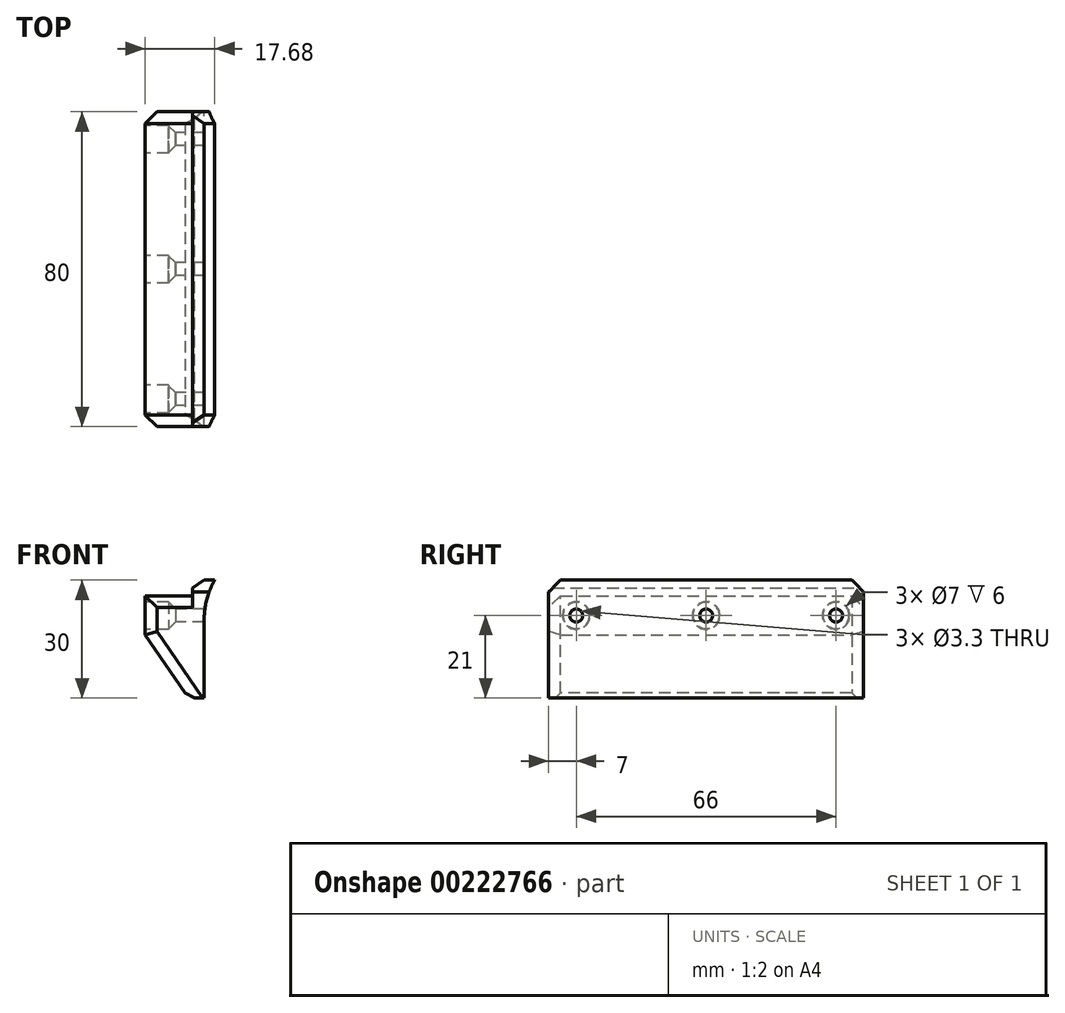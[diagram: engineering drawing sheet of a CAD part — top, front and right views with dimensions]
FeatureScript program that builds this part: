
annotation { "Feature Type Name" : "Feature", "Feature Type Description" : "" }
export const myFeature = defineFeature(function(context is Context, id is Id, definition is map)
    precondition{}
    {
        {
            var Q0;
            Q0=qCreatedBy(makeId("Front.planeOp"),FACE);
            var sketch = newSketch(context, id + "F0", { "sketchPlane" : qUnion([Q0])});
            skLineSegment(sketch, "E0", {"start": v(0, 0) * mm, "end": v(-15, 0) * mm});
            skLineSegment(sketch, "E1", {"start": v(-15, 0) * mm, "end": v(-15, -10) * mm});
            skLineSegment(sketch, "E2", {"start": v(-15, -10) * mm, "end": v(-4, -26) * mm});
            skLineSegment(sketch, "E3", {"start": v(-4, -26) * mm, "end": v(0, -26) * mm});
            skLineSegment(sketch, "E4", {"start": v(0, -26) * mm, "end": v(0, 0) * mm});
            skSolve(sketch);
        }
        {
            var Q0;
            Q0=makeQuery(id+"F0.imprint","IMPRINT",FACE,{"disambiguationData":[TD([[makeQuery(id+"F0.imprint","IMPRINT",EDGE,{"derivedFrom":sQuery(id+"F0.wireOp",EDGE,"E0")}),1.0]])]});
            extrude(context, id + "F1", {"entities" : qUnion([Q0]), "endBound" : BoundingType.SYMMETRIC, "depth" : 80 * mm});
        }
        {
            var Q0;
            Q0=makeQuery(id+"F1.opExtrude","SWEPT_FACE",FACE,{"disambiguationData":[OSD([sQuery(id+"F0.wireOp",EDGE,"E1")])]});
            var sketch = newSketch(context, id + "F2", { "sketchPlane" : qUnion([Q0])});
            skLineSegment(sketch, "E5.0", {"start": v(40, 0) * mm, "end": v(-40, 0) * mm, "construction": true});
            skCircle(sketch, "E6", {"center": v(-33, -5) * mm, "radius": 3.5 * mm});
            skCircle(sketch, "E7", {"center": v(33, -5) * mm, "radius": 3.5 * mm});
            skCircle(sketch, "E8", {"center": v(0, -5) * mm, "radius": 3.5 * mm});
            skSolve(sketch);
        }
        {
            var Q0;
            Q0=qCreatedBy(makeId("Front.planeOp"),FACE);
            var sketch = newSketch(context, id + "F3", { "sketchPlane" : qUnion([Q0])});
            skArc(sketch, "E9", {"start": v(2.68, 4) * mm, "mid": v(0.68, -0.82) * mm, "end": v(0, -6) * mm});
            skLineSegment(sketch, "E10", {"start": v(2.68, 4) * mm, "end": v(0, 4) * mm});
            skLineSegment(sketch, "E11", {"start": v(0, 4) * mm, "end": v(-3, 2) * mm});
            skLineSegment(sketch, "E12", {"start": v(0, 0) * mm, "end": v(0, -6) * mm});
            skLineSegment(sketch, "E13", {"start": v(-3, 2) * mm, "end": v(-3, 0) * mm});
            skLineSegment(sketch, "E14", {"start": v(-3, 0) * mm, "end": v(0, 0) * mm});
            skSolve(sketch);
        }
        {
            var Q0;
            Q0=qSketchRegion(id+"F2",true);
            extrude(context, id + "F4", {"entities" : qUnion([Q0]), "operationType" : NewBodyOperationType.REMOVE, "oppositeDirection" : true, "depth" : 6 * mm});
        }
        {
            var Q0;
            Q0 = qSketchRegion(id + "F3", true);
            var Q1;
            Q1=makeQuery(id+"F1.opExtrude","CAP_FACE",FACE,{"disambiguationData":[OSD([sQuery(id+"F0.wireOp",EDGE,"E0"),sQuery(id+"F0.wireOp",EDGE,"E1"),sQuery(id+"F0.wireOp",EDGE,"E2"),sQuery(id+"F0.wireOp",EDGE,"E3"),sQuery(id+"F0.wireOp",EDGE,"E4")])],"isStart":true});
            var Q2;
            Q2=makeQuery(id+"F1.opExtrude","CAP_FACE",FACE,{"disambiguationData":[OSD([sQuery(id+"F0.wireOp",EDGE,"E0"),sQuery(id+"F0.wireOp",EDGE,"E1"),sQuery(id+"F0.wireOp",EDGE,"E2"),sQuery(id+"F0.wireOp",EDGE,"E3"),sQuery(id+"F0.wireOp",EDGE,"E4")])],"isStart":false});
            extrude(context, id + "F5", {"entities" : qUnion([Q0]), "operationType" : NewBodyOperationType.ADD, "endBound" : BoundingType.SYMMETRIC, "endBoundEntityFace" : qUnion([Q1]), "depth" : 80 * mm, "hasSecondDirection" : true, "secondDirectionBound" : SecondDirectionBoundingType.UP_TO_SURFACE, "secondDirectionOppositeDirection" : true, "secondDirectionBoundEntityFace" : qUnion([Q2]), "secondDirectionDepth" : 25 * mm});
        }
        {
            var Q0;
            Q0=makeQuery(id+"F4.boolean.opBoolean","COPY",FACE,{"derivedFrom":makeQuery(id+"F4.opExtrude","CAP_FACE",FACE,{"disambiguationData":[OSD([sQuery(id+"F2.wireOp",EDGE,"E7")])],"isStart":false})});
            var sketch = newSketch(context, id + "F6", { "sketchPlane" : qUnion([Q0])});
            skPoint(sketch, "E15", {"position": v(-33, -5) * mm});
            skPoint(sketch, "E16", {"position": v(0, -5) * mm});
            skPoint(sketch, "E17", {"position": v(33, -5) * mm});
            skSolve(sketch);
        }
        {
            var Q0;
            Q0=sQuery(id+"F6.wireOp",VERTEX,"E16");
            var Q1;
            Q1=sQuery(id+"F6.wireOp",VERTEX,"E17");
            var Q2;
            Q2=sQuery(id+"F6.wireOp",VERTEX,"E15");
            var Q3;
            Q3=sQuery(id+"F6.wireOp",VERTEX,"b85a0811-0142-4255-a70c-24b2cf59c3c1");
            var Q4;
            Q4=makeQuery(id+"F1.opExtrude","SWEPT_BODY",BODY,{"disambiguationData":[OSD([sQuery(id+"F0.wireOp",EDGE,"E0"),sQuery(id+"F0.wireOp",EDGE,"E1"),sQuery(id+"F0.wireOp",EDGE,"E2"),sQuery(id+"F0.wireOp",EDGE,"E3"),sQuery(id+"F0.wireOp",EDGE,"E4")])]});
            hole(context, id + "F7", {"style" : HoleStyle.C_SINK, "endStyle" : HoleEndStyle.THROUGH, "standardTappedOrClearance" : lookupTablePath({ "standard" : "ISO", "fit" : "Normal", "size" : "M3", "type" : "Clearance" }), "standardBlindInLast" : lookupTablePath({ "fit" : "Standard", "standard" : "ISO", "size" : "M3", "type" : "Clearance" }), "holeDiameter" : 3.3 * mm, "cSinkDiameter" : 6.72 * mm, "cSinkAngle" : 90 * degree, "locations" : qUnion([Q0, Q1, Q2, Q3]), "scope" : qUnion([Q4]), "isTappedThrough" : true});
        }
        {
            var Q0;
            Q0=makeQuery(id+"F1.opExtrude","CAP_EDGE",EDGE,{"disambiguationData":[OSD([sQuery(id+"F0.wireOp",EDGE,"E0")])],"isStart":false});
            var Q1;
            Q1=makeQuery(id+"F1.opExtrude","CAP_EDGE",EDGE,{"disambiguationData":[OSD([sQuery(id+"F0.wireOp",EDGE,"E0")])],"isStart":true});
            var Q2;
            Q2=makeQuery(id+"F1.opExtrude","CAP_EDGE",EDGE,{"disambiguationData":[OSD([sQuery(id+"F0.wireOp",EDGE,"E1")])],"isStart":true});
            var Q3;
            Q3=makeQuery(id+"F1.opExtrude","CAP_EDGE",EDGE,{"disambiguationData":[OSD([sQuery(id+"F0.wireOp",EDGE,"E1")])],"isStart":false});
            var Q4;
            Q4=makeQuery(id+"F1.opExtrude","CAP_EDGE",EDGE,{"disambiguationData":[OSD([sQuery(id+"F0.wireOp",EDGE,"E2")])],"isStart":false});
            var Q5;
            Q5=makeQuery(id+"F1.opExtrude","CAP_EDGE",EDGE,{"disambiguationData":[OSD([sQuery(id+"F0.wireOp",EDGE,"E2")])],"isStart":true});
            var Q6;
            Q6=makeQuery(id+"F1.opExtrude","SWEPT_EDGE",EDGE,{"disambiguationData":[OSD([sQuery(id+"F0.wireOp",EDGE,"E2"),sQuery(id+"F0.wireOp",EDGE,"E3")])]});
            var Q7;
            Q7=makeQuery(id+"F5.opExtrude","CAP_EDGE",EDGE,{"disambiguationData":[OSD([sQuery(id+"F3.wireOp",EDGE,"E10")])],"isStart":false});
            var Q8;
            Q8=makeQuery(id+"F5.opExtrude","CAP_EDGE",EDGE,{"disambiguationData":[OSD([sQuery(id+"F3.wireOp",EDGE,"E10")])],"isStart":true});
            chamfer(context, id + "F8", {"entities" : qUnion([Q0, Q1, Q2, Q3, Q4, Q5, Q6, Q7, Q8]), "width" : 3 * mm, "tangentPropagation" : true});
        }
    });
